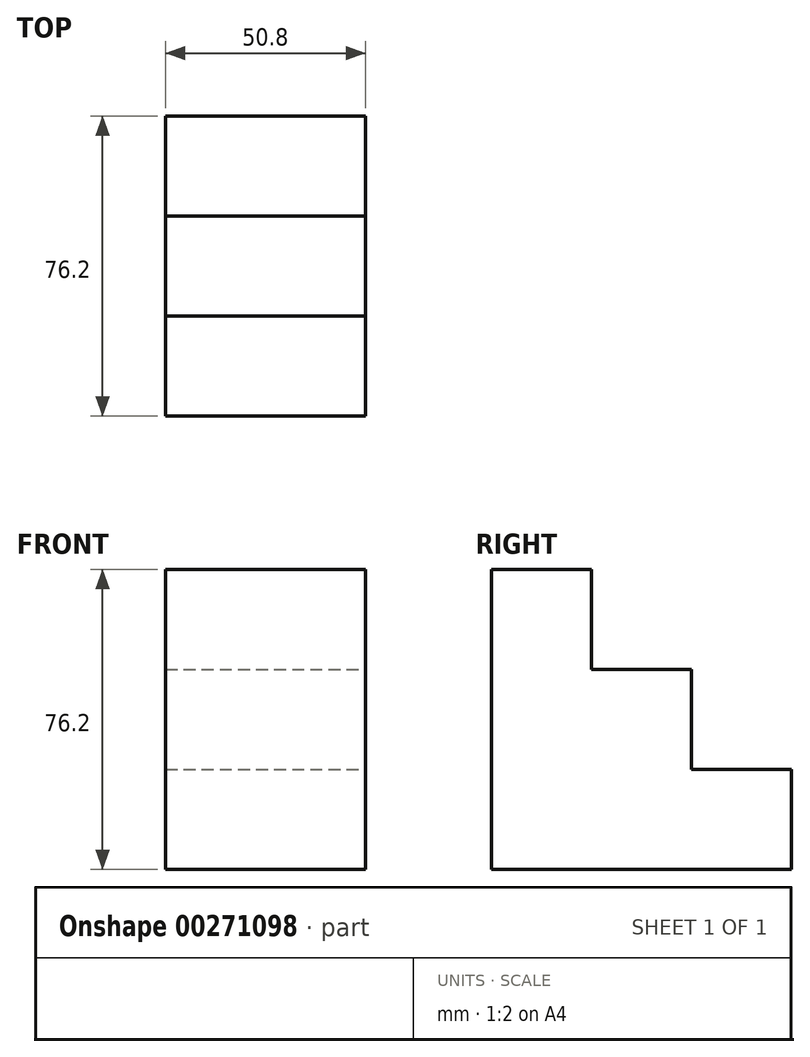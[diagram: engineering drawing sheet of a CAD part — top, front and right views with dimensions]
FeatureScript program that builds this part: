
annotation { "Feature Type Name" : "Feature", "Feature Type Description" : "" }
export const myFeature = defineFeature(function(context is Context, id is Id, definition is map)
    precondition{}
    {
        {
            var Q0;
            Q0=qCreatedBy(makeId("Front.planeOp"),FACE);
            var sketch = newSketch(context, id + "F0", { "sketchPlane" : qUnion([Q0])});
            skLineSegment(sketch, "E0.bottom", {"start": v(0, 0) * mm, "end": v(50.8, 0) * mm});
            skLineSegment(sketch, "E0.top", {"start": v(0, 76.2) * mm, "end": v(50.8, 76.2) * mm});
            skLineSegment(sketch, "E0.left", {"start": v(0, 0) * mm, "end": v(0, 76.2) * mm});
            skLineSegment(sketch, "E0.right", {"start": v(50.8, 0) * mm, "end": v(50.8, 76.2) * mm});
            skSolve(sketch);
        }
        {
            var Q0;
            Q0=makeQuery(id+"F0.imprint","IMPRINT",FACE,{"disambiguationData":[TD([[makeQuery(id+"F0.imprint","IMPRINT",EDGE,{"derivedFrom":sQuery(id+"F0.wireOp",EDGE,"E0.bottom")}),1.0]])]});
            extrude(context, id + "F1", {"entities" : qUnion([Q0]), "depth" : 25.4 * mm});
        }
        {
            var Q0;
            Q0=qCreatedBy(makeId("Front.planeOp"),FACE);
            var sketch = newSketch(context, id + "F2", { "sketchPlane" : qUnion([Q0])});
            skLineSegment(sketch, "E1.bottom", {"start": v(0, 0) * mm, "end": v(50.8, 0) * mm});
            skLineSegment(sketch, "E1.top", {"start": v(0, 50.8) * mm, "end": v(50.8, 50.8) * mm});
            skLineSegment(sketch, "E1.left", {"start": v(0, 0) * mm, "end": v(0, 50.8) * mm});
            skLineSegment(sketch, "E1.right", {"start": v(50.8, 0) * mm, "end": v(50.8, 50.8) * mm});
            skSolve(sketch);
        }
        {
            var Q0;
            Q0 = qSketchRegion(id + "F2", true);
            var Q1;
            Q1=makeQuery(id+"F1.opExtrude","CAP_FACE",FACE,{"disambiguationData":[OSD([sQuery(id+"F0.wireOp",EDGE,"E0.bottom"),sQuery(id+"F0.wireOp",EDGE,"E0.top"),sQuery(id+"F0.wireOp",EDGE,"E0.left"),sQuery(id+"F0.wireOp",EDGE,"E0.right")])],"isStart":false});
            extrude(context, id + "F3", {"entities" : qUnion([Q0, Q1]), "operationType" : NewBodyOperationType.ADD, "oppositeDirection" : true, "depth" : 25.4 * mm});
        }
        {
            var Q0;
            Q0=qCreatedBy(makeId("Front.planeOp"),FACE);
            var sketch = newSketch(context, id + "F4", { "sketchPlane" : qUnion([Q0])});
            skLineSegment(sketch, "E2.bottom", {"start": v(0, 0) * mm, "end": v(50.8, 0) * mm});
            skLineSegment(sketch, "E2.top", {"start": v(0, 25.4) * mm, "end": v(50.8, 25.4) * mm});
            skLineSegment(sketch, "E2.left", {"start": v(0, 0) * mm, "end": v(0, 25.4) * mm});
            skLineSegment(sketch, "E2.right", {"start": v(50.8, 0) * mm, "end": v(50.8, 25.4) * mm});
            skSolve(sketch);
        }
        {
            var Q0;
            Q0 = qSketchRegion(id + "F4", true);
            extrude(context, id + "F5", {"entities" : qUnion([Q0]), "operationType" : NewBodyOperationType.ADD, "oppositeDirection" : true, "depth" : 50.8 * mm});
        }
    });
